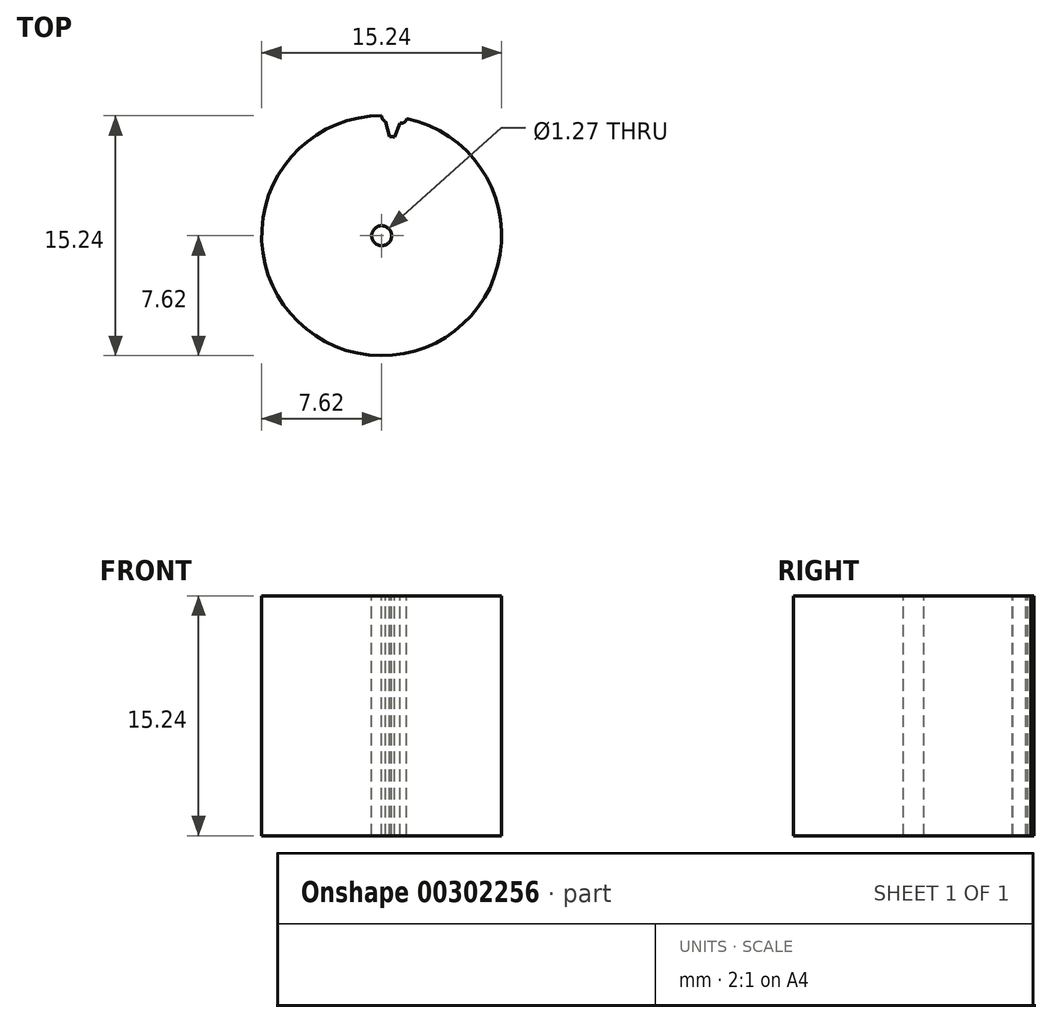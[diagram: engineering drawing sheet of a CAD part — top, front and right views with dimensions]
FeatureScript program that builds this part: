
annotation { "Feature Type Name" : "Feature", "Feature Type Description" : "" }
export const myFeature = defineFeature(function(context is Context, id is Id, definition is map)
    precondition{}
    {
        {
            var Q0;
            Q0=qCreatedBy(makeId("Top.planeOp"),FACE);
            var sketch = newSketch(context, id + "F0", { "sketchPlane" : qUnion([Q0])});
            skCircle(sketch, "E0", {"center": v(0, 0) * mm, "radius": 7.62 * mm});
            skSolve(sketch);
        }
        {
            var Q0;
            Q0 = qSketchRegion(id + "F0", true);
            extrude(context, id + "F1", {"entities" : qUnion([Q0]), "endBound" : BoundingType.SYMMETRIC, "depth" : 15.24 * mm});
        }
        {
            var Q0;
            Q0=makeQuery(id+"F1.opExtrude","CAP_FACE",FACE,{"disambiguationData":[OSD([sQuery(id+"F0.wireOp",EDGE,"E0")])],"isStart":false});
            var sketch = newSketch(context, id + "F2", { "sketchPlane" : qUnion([Q0])});
            skCircle(sketch, "E1", {"center": v(0, 0) * mm, "radius": 0.64 * mm});
            skSolve(sketch);
        }
        {
            var Q0;
            Q0 = qSketchRegion(id + "F2", true);
            var Q1;
            Q1=makeQuery(id+"F1.opExtrude","CAP_FACE",FACE,{"disambiguationData":[OSD([sQuery(id+"F0.wireOp",EDGE,"E0")])],"isStart":true});
            extrude(context, id + "F3", {"entities" : qUnion([Q0]), "operationType" : NewBodyOperationType.REMOVE, "endBound" : BoundingType.UP_TO_SURFACE, "oppositeDirection" : true, "endBoundEntityFace" : qUnion([Q1]), "depth" : 25.4 * mm});
        }
        {
            var Q0;
            Q0=makeQuery(id+"F1.opExtrude","CAP_FACE",FACE,{"disambiguationData":[OSD([sQuery(id+"F0.wireOp",EDGE,"E0")])],"isStart":false});
            var sketch = newSketch(context, id + "F4", { "sketchPlane" : qUnion([Q0])});
            skLineSegment(sketch, "E2", {"start": v(0, 9.03) * mm, "end": v(0, -9.08) * mm, "construction": true});
            skCircle(sketch, "E3", {"center": v(0, -0.02) * mm, "radius": 6.35 * mm, "construction": true});
            skLineSegment(sketch, "E4", {"start": v(-1.98, -9.34) * mm, "end": v(2.37, 11.13) * mm, "construction": true});
            skArc(sketch, "E5", {"start": v(1.59, 7.45) * mm, "mid": v(0.8, 7.58) * mm, "end": v(0, 7.62) * mm});
            skArc(sketch, "E6", {"start": v(0.5, 6.3) * mm, "mid": v(0.66, 6.3) * mm, "end": v(0.82, 6.27) * mm});
            skArc(sketch, "E7", {"start": v(0, 7.62) * mm, "mid": v(0.07, 7.4) * mm, "end": v(0.26, 7.25) * mm});
            skArc(sketch, "E8", {"start": v(1.59, 7.45) * mm, "mid": v(1.44, 7.22) * mm, "end": v(1.18, 7.14) * mm});
            skLineSegment(sketch, "E9", {"start": v(0.26, 7.25) * mm, "end": v(0.5, 6.3) * mm});
            skLineSegment(sketch, "E10", {"start": v(1.18, 7.14) * mm, "end": v(0.82, 6.27) * mm});
            skSolve(sketch);
        }
        {
            var Q0;
            Q0 = qSketchRegion(id + "F4", true);
            var Q1;
            Q1=makeQuery(id+"F1.opExtrude","CAP_FACE",FACE,{"disambiguationData":[OSD([sQuery(id+"F0.wireOp",EDGE,"E0")])],"isStart":true});
            extrude(context, id + "F5", {"entities" : qUnion([Q0]), "operationType" : NewBodyOperationType.REMOVE, "endBound" : BoundingType.UP_TO_SURFACE, "oppositeDirection" : true, "endBoundEntityFace" : qUnion([Q1]), "depth" : 25.4 * mm});
        }
        {
            var Q0;
            Q0=qCreatedBy(makeId("Right.planeOp"),FACE);
            var sketch = newSketch(context, id + "F6", { "sketchPlane" : qUnion([Q0])});
            skLineSegment(sketch, "E11", {"start": v(0, 28.4) * mm, "end": v(0, -25.44) * mm, "construction": true});
            skSolve(sketch);
        }
    });
